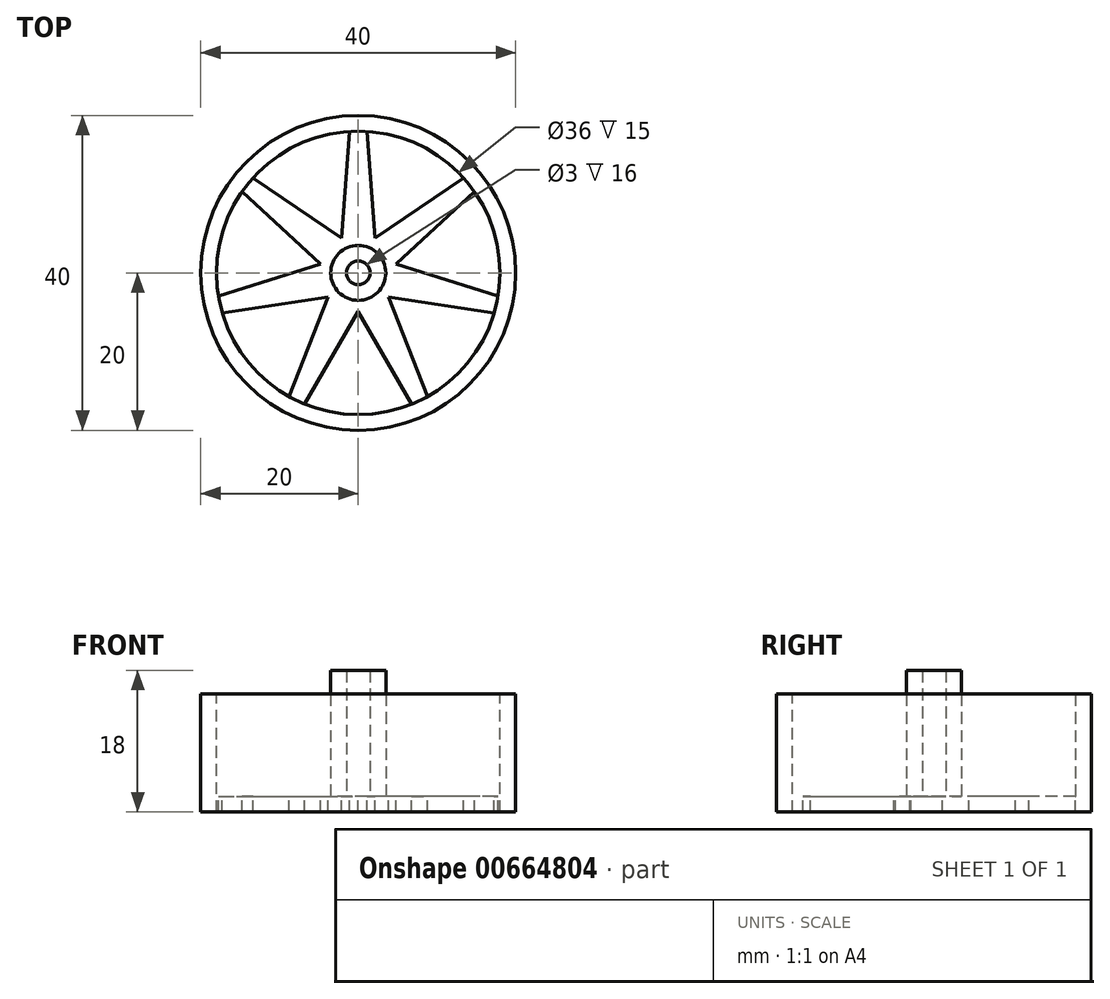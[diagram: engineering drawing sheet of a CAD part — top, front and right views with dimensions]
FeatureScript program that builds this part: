
annotation { "Feature Type Name" : "Feature", "Feature Type Description" : "" }
export const myFeature = defineFeature(function(context is Context, id is Id, definition is map)
    precondition{}
    {
        {
            var Q0;
            Q0=qCreatedBy(makeId("Top.planeOp"),FACE);
            var sketch = newSketch(context, id + "F0", { "sketchPlane" : qUnion([Q0])});
            skCircle(sketch, "E0", {"center": v(0, 0) * mm, "radius": 20 * mm});
            skSolve(sketch);
        }
        {
            var Q0;
            Q0=makeQuery(id+"F0.imprint","IMPRINT",FACE,{"disambiguationData":[TD([[makeQuery(id+"F0.imprint","IMPRINT",EDGE,{"derivedFrom":sQuery(id+"F0.wireOp",EDGE,"E0")}),1.0]])]});
            extrude(context, id + "F1", {"entities" : qUnion([Q0]), "depth" : 15 * mm});
        }
        {
            var Q0;
            Q0=makeQuery(id+"F1.opExtrude","CAP_FACE",FACE,{"disambiguationData":[OSD([sQuery(id+"F0.wireOp",EDGE,"E0")])],"isStart":false});
            var sketch = newSketch(context, id + "F2", { "sketchPlane" : qUnion([Q0])});
            skCircle(sketch, "E1", {"center": v(0, 0) * mm, "radius": 18 * mm});
            skSolve(sketch);
        }
        {
            var Q0;
            Q0=makeQuery(id+"F2.imprint","IMPRINT",FACE,{"disambiguationData":[TD([[makeQuery(id+"F2.imprint","IMPRINT",EDGE,{"derivedFrom":sQuery(id+"F2.wireOp",EDGE,"E1")}),1.0]])]});
            extrude(context, id + "F3", {"entities" : qUnion([Q0]), "operationType" : NewBodyOperationType.REMOVE, "oppositeDirection" : true, "depth" : 13 * mm});
        }
        {
            var Q0;
            Q0=makeQuery(id+"F3.boolean.opBoolean","COPY",FACE,{"derivedFrom":makeQuery(id+"F3.opExtrude","CAP_FACE",FACE,{"disambiguationData":[OSD([sQuery(id+"F2.wireOp",EDGE,"E1")])],"isStart":false})});
            var sketch = newSketch(context, id + "F4", { "sketchPlane" : qUnion([Q0])});
            skSolve(sketch);
        }
        {
            var Q0;
            Q0=makeQuery(id+"F4.imprint","IMPRINT",FACE,{"disambiguationData":[TD([[makeQuery(id+"F4.imprint","IMPRINT",EDGE,{"derivedFrom":makeQuery(id+"F3.boolean.opBoolean","COPY",EDGE,{"derivedFrom":makeQuery(id+"F3.opExtrude","CAP_EDGE",EDGE,{"disambiguationData":[OSD([sQuery(id+"F2.wireOp",EDGE,"E1")])],"isStart":false})})}),1.0]])]});
            var sketch = newSketch(context, id + "F5", { "sketchPlane" : qUnion([Q0])});
            skCircle(sketch, "E2", {"center": v(0, 0) * mm, "radius": 3.5 * mm});
            skCircle(sketch, "E3", {"center": v(0, 0) * mm, "radius": 1.5 * mm});
            skSolve(sketch);
        }
        {
            var Q0;
            Q0=qSketchRegion(id+"F5",true);
            extrude(context, id + "F6", {"entities" : qUnion([Q0]), "operationType" : NewBodyOperationType.ADD, "depth" : 16 * mm});
        }
        {
            var Q0;
            Q0=makeQuery(id+"F4.imprint","IMPRINT",FACE,{"disambiguationData":[TD([[makeQuery(id+"F4.imprint","IMPRINT",EDGE,{"derivedFrom":makeQuery(id+"F3.boolean.opBoolean","COPY",EDGE,{"derivedFrom":makeQuery(id+"F3.opExtrude","CAP_EDGE",EDGE,{"disambiguationData":[OSD([sQuery(id+"F2.wireOp",EDGE,"E1")])],"isStart":false})})}),1.0]])]});
            var sketch = newSketch(context, id + "F7", { "sketchPlane" : qUnion([Q0])});
            skLineSegment(sketch, "E4", {"start": v(-1.1, 18.07) * mm, "end": v(-2.3, 2.18) * mm});
            skLineSegment(sketch, "E5.MirrorCS", {"start": v(1.1, 18.07) * mm, "end": v(2.3, 2.18) * mm});
            skLineSegment(sketch, "E6.1.0", {"start": v(-13.44, 12.13) * mm, "end": v(-0.27, 3.16) * mm});
            skLineSegment(sketch, "E6.1.1", {"start": v(-14.82, 10.4) * mm, "end": v(-3.14, -0.44) * mm});
            skLineSegment(sketch, "E6.2.0", {"start": v(-17.87, -2.94) * mm, "end": v(-2.64, 1.76) * mm});
            skLineSegment(sketch, "E6.2.1", {"start": v(-17.37, -5.1) * mm, "end": v(-1.62, -2.73) * mm});
            skLineSegment(sketch, "E6.3.0", {"start": v(-8.84, -15.8) * mm, "end": v(-3.02, -0.97) * mm});
            skLineSegment(sketch, "E6.3.1", {"start": v(-6.85, -16.76) * mm, "end": v(1.13, -2.97) * mm});
            skLineSegment(sketch, "E6.4.0", {"start": v(6.85, -16.76) * mm, "end": v(-1.13, -2.97) * mm});
            skLineSegment(sketch, "E6.4.1", {"start": v(8.84, -15.8) * mm, "end": v(3.02, -0.97) * mm});
            skLineSegment(sketch, "E6.5.0", {"start": v(17.37, -5.1) * mm, "end": v(1.62, -2.73) * mm});
            skLineSegment(sketch, "E6.5.1", {"start": v(17.87, -2.94) * mm, "end": v(2.64, 1.76) * mm});
            skLineSegment(sketch, "E6.6.0", {"start": v(14.82, 10.4) * mm, "end": v(3.14, -0.44) * mm});
            skLineSegment(sketch, "E6.6.1", {"start": v(13.44, 12.13) * mm, "end": v(0.27, 3.16) * mm});
            skPoint(sketch, "E6.center", {"position": v(0, 0) * mm});
            skCircle(sketch, "E7", {"center": v(0, 0) * mm, "radius": 18 * mm});
            skSolve(sketch);
        }
        {
            var Q0;
            {var subQ0=sQuery(id+"F7.wireOp",EDGE,"E6.3.0");var subQ1=sQuery(id+"F7.wireOp",EDGE,"E6.2.1");var subQ2=makeQuery(id+"F7.imprint","INTERSECT",VERTEX,{"derivedFrom":[subQ1,subQ0]});Q0=makeQuery(id+"F7.imprint","IMPRINT",FACE,{"disambiguationData":[TD([[makeQuery(id+"F7.imprint","IMPRINT",EDGE,{"disambiguationData":[TD([[subQ2,1.0]])],"derivedFrom":subQ1}),-1.0]])]});}
            var Q1;
            {var subQ0=sQuery(id+"F7.wireOp",EDGE,"E6.4.0");var subQ1=sQuery(id+"F7.wireOp",EDGE,"E6.3.1");var subQ2=makeQuery(id+"F7.imprint","INTERSECT",VERTEX,{"derivedFrom":[subQ1,subQ0]});Q1=makeQuery(id+"F7.imprint","IMPRINT",FACE,{"disambiguationData":[TD([[makeQuery(id+"F7.imprint","IMPRINT",EDGE,{"disambiguationData":[TD([[subQ2,1.0]])],"derivedFrom":subQ1}),-1.0]])]});}
            var Q2;
            {var subQ0=sQuery(id+"F7.wireOp",EDGE,"E6.2.0");var subQ1=sQuery(id+"F7.wireOp",EDGE,"E6.1.1");var subQ2=makeQuery(id+"F7.imprint","INTERSECT",VERTEX,{"derivedFrom":[subQ1,subQ0]});Q2=makeQuery(id+"F7.imprint","IMPRINT",FACE,{"disambiguationData":[TD([[makeQuery(id+"F7.imprint","IMPRINT",EDGE,{"disambiguationData":[TD([[subQ2,1.0]])],"derivedFrom":subQ1}),-1.0]])]});}
            var Q3;
            {var subQ0=sQuery(id+"F7.wireOp",EDGE,"E6.1.0");var subQ1=sQuery(id+"F7.wireOp",EDGE,"E4");var subQ2=makeQuery(id+"F7.imprint","INTERSECT",VERTEX,{"derivedFrom":[subQ1,subQ0]});Q3=makeQuery(id+"F7.imprint","IMPRINT",FACE,{"disambiguationData":[TD([[makeQuery(id+"F7.imprint","IMPRINT",EDGE,{"disambiguationData":[TD([[subQ2,1.0]])],"derivedFrom":subQ1}),-1.0]])]});}
            var Q4;
            {var subQ0=sQuery(id+"F7.wireOp",EDGE,"E6.6.1");var subQ1=sQuery(id+"F7.wireOp",EDGE,"E5.MirrorCS");var subQ2=makeQuery(id+"F7.imprint","INTERSECT",VERTEX,{"derivedFrom":[subQ1,subQ0]});Q4=makeQuery(id+"F7.imprint","IMPRINT",FACE,{"disambiguationData":[TD([[makeQuery(id+"F7.imprint","IMPRINT",EDGE,{"disambiguationData":[TD([[subQ2,1.0]])],"derivedFrom":subQ1}),1.0]])]});}
            var Q5;
            {var subQ0=sQuery(id+"F7.wireOp",EDGE,"E6.6.0");var subQ1=sQuery(id+"F7.wireOp",EDGE,"E6.5.1");var subQ2=makeQuery(id+"F7.imprint","INTERSECT",VERTEX,{"derivedFrom":[subQ1,subQ0]});Q5=makeQuery(id+"F7.imprint","IMPRINT",FACE,{"disambiguationData":[TD([[makeQuery(id+"F7.imprint","IMPRINT",EDGE,{"disambiguationData":[TD([[subQ2,1.0]])],"derivedFrom":subQ1}),-1.0]])]});}
            var Q6;
            {var subQ0=sQuery(id+"F7.wireOp",EDGE,"E6.5.0");var subQ1=sQuery(id+"F7.wireOp",EDGE,"E6.4.1");var subQ2=makeQuery(id+"F7.imprint","INTERSECT",VERTEX,{"derivedFrom":[subQ1,subQ0]});Q6=makeQuery(id+"F7.imprint","IMPRINT",FACE,{"disambiguationData":[TD([[makeQuery(id+"F7.imprint","IMPRINT",EDGE,{"disambiguationData":[TD([[subQ2,1.0]])],"derivedFrom":subQ1}),-1.0]])]});}
            extrude(context, id + "F8", {"entities" : qUnion([Q0, Q1, Q2, Q3, Q4, Q5, Q6]), "operationType" : NewBodyOperationType.REMOVE, "oppositeDirection" : true, "depth" : 2 * mm});
        }
    });
